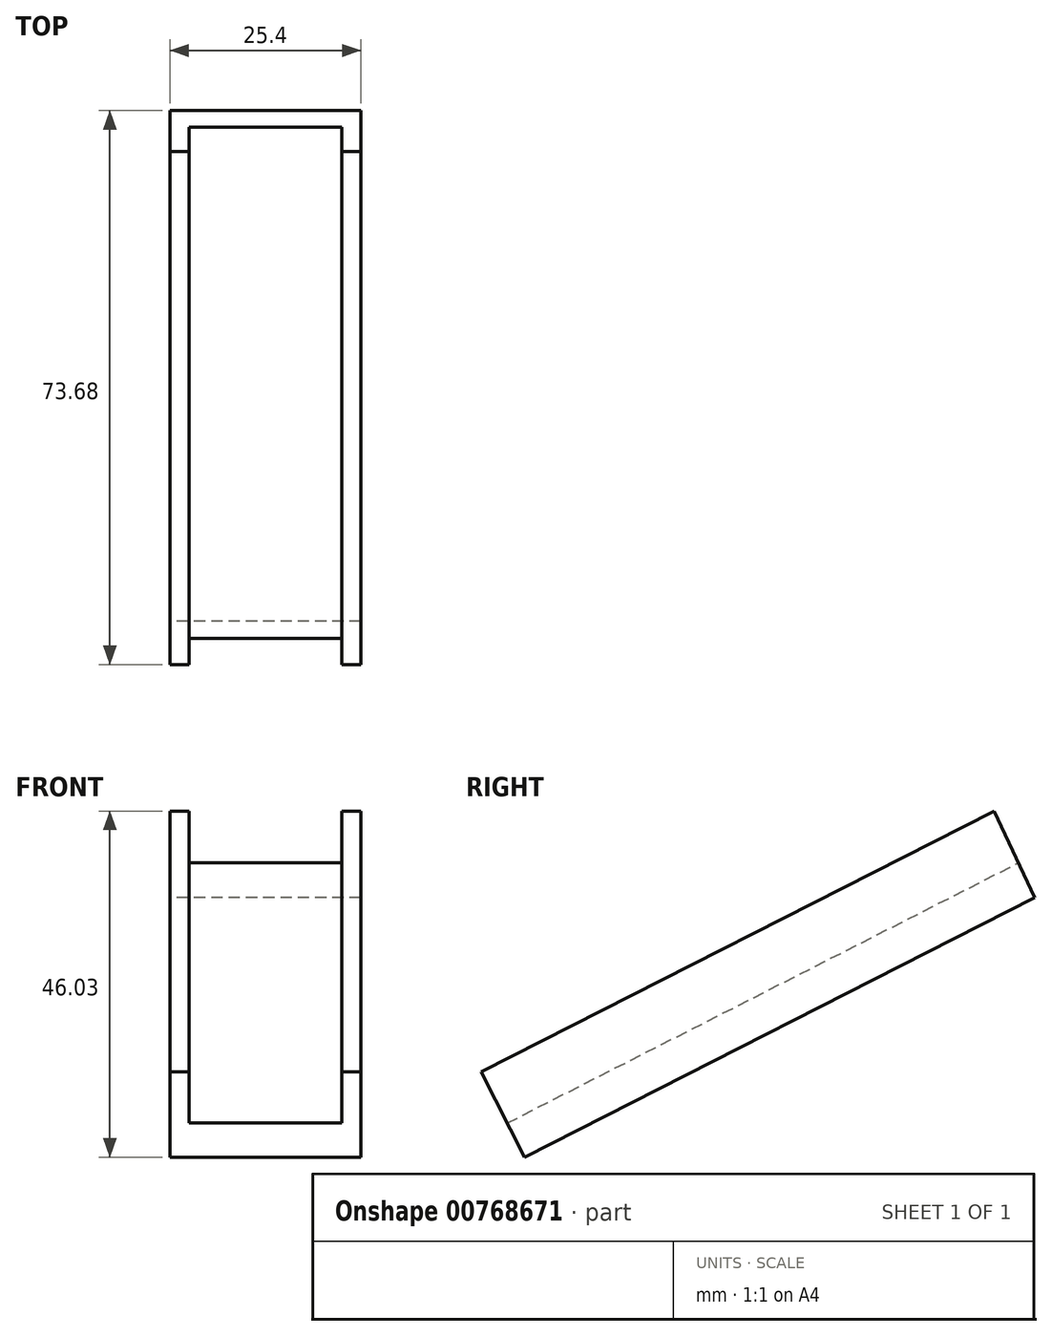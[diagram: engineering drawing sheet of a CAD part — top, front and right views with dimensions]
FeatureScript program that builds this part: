
annotation { "Feature Type Name" : "Feature", "Feature Type Description" : "" }
export const myFeature = defineFeature(function(context is Context, id is Id, definition is map)
    precondition{}
    {
        {
            var Q0;
            Q0=qCreatedBy(makeId("Right.planeOp"),FACE);
            var sketch = newSketch(context, id + "F0", { "sketchPlane" : qUnion([Q0])});
            skLineSegment(sketch, "E0", {"start": v(0, 0) * mm, "end": v(67.92, 34.55) * mm});
            skLineSegment(sketch, "E1", {"start": v(0, 0) * mm, "end": v(-5.76, 11.32) * mm});
            skLineSegment(sketch, "E2", {"start": v(-5.76, 11.32) * mm, "end": v(62.48, 46.03) * mm});
            skLineSegment(sketch, "E3", {"start": v(62.48, 46.03) * mm, "end": v(67.92, 34.55) * mm});
            skSolve(sketch);
        }
        {
            var Q0;
            Q0=qSketchRegion(id+"F0",true);
            extrude(context, id + "F1", {"entities" : qUnion([Q0]), "depth" : 25.4 * mm, "offsetDistance" : 25.4 * mm});
        }
        {
            var Q0;
            Q0=makeQuery(id+"F1.opExtrude","SWEPT_FACE",FACE,{"disambiguationData":[OSD([sQuery(id+"F0.wireOp",EDGE,"E2")])]});
            var sketch = newSketch(context, id + "F2", { "sketchPlane" : qUnion([Q0])});
            skLineSegment(sketch, "E4", {"start": v(2.54, 0) * mm, "end": v(2.54, 76.56) * mm});
            skLineSegment(sketch, "E5", {"start": v(2.54, 76.56) * mm, "end": v(22.86, 76.56) * mm});
            skLineSegment(sketch, "E6", {"start": v(22.86, 76.56) * mm, "end": v(22.86, 0) * mm});
            skSolve(sketch);
        }
        {
            var Q0;
            Q0=qSketchRegion(id+"F2",true);
            var Q1;
            {var subQ0=sQuery(id+"F2.wireOp",EDGE,"E4");Q1=makeQuery(id+"F2.imprint","IMPRINT",FACE,{"disambiguationData":[TD([[makeQuery(id+"F2.imprint","IMPRINT",EDGE,{"derivedFrom":subQ0}),-1.0]])]});}
            extrude(context, id + "F3", {"entities" : qUnion([Q0, Q1]), "operationType" : NewBodyOperationType.REMOVE, "oppositeDirection" : true, "depth" : 7.62 * mm, "offsetDistance" : 25.4 * mm});
        }
    });
